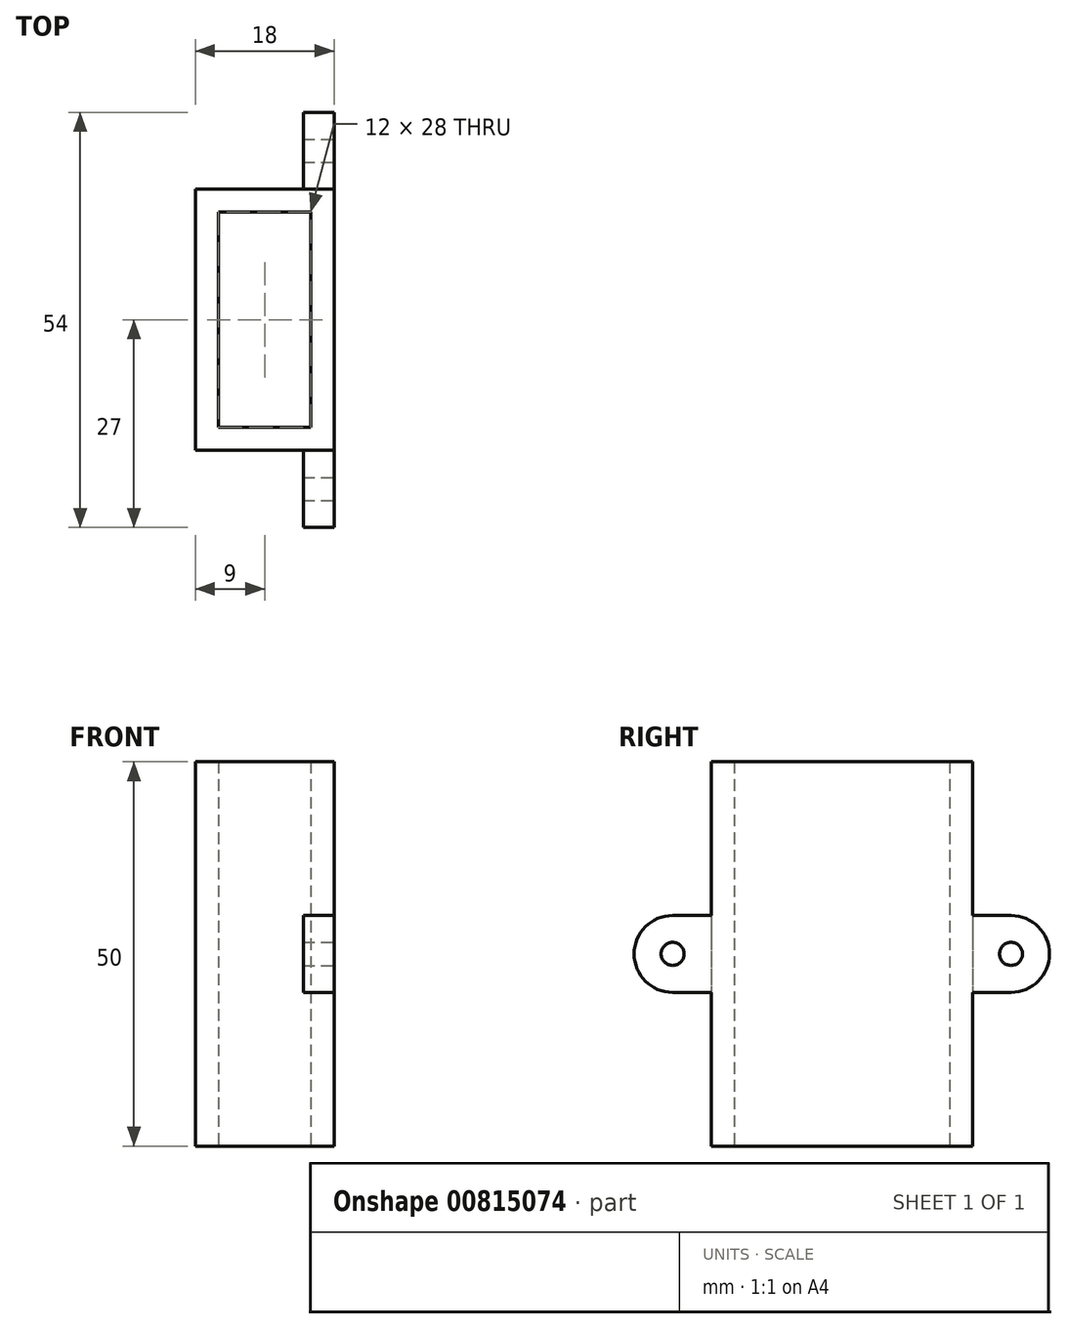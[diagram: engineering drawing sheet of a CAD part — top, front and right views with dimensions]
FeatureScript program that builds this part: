
annotation { "Feature Type Name" : "Feature", "Feature Type Description" : "" }
export const myFeature = defineFeature(function(context is Context, id is Id, definition is map)
    precondition{}
    {
        {
            var Q0;
            Q0=qCreatedBy(makeId("Top.planeOp"),FACE);
            var sketch = newSketch(context, id + "F0", { "sketchPlane" : qUnion([Q0])});
            skLineSegment(sketch, "E0.bottom", {"start": v(6, -14) * mm, "end": v(-6, -14) * mm});
            skLineSegment(sketch, "E0.top", {"start": v(6, 14) * mm, "end": v(-6, 14) * mm});
            skLineSegment(sketch, "E0.left", {"start": v(6, -14) * mm, "end": v(6, 14) * mm});
            skLineSegment(sketch, "E0.right", {"start": v(-6, -14) * mm, "end": v(-6, 14) * mm});
            skPoint(sketch, "E0.middle", {"position": v(0, 0) * mm});
            skLineSegment(sketch, "E1.bottom", {"start": v(9, -17) * mm, "end": v(-9, -17) * mm});
            skLineSegment(sketch, "E1.top", {"start": v(9, 17) * mm, "end": v(-9, 17) * mm});
            skLineSegment(sketch, "E1.left", {"start": v(9, -17) * mm, "end": v(9, 17) * mm});
            skLineSegment(sketch, "E1.right", {"start": v(-9, -17) * mm, "end": v(-9, 17) * mm});
            skLineSegment(sketch, "E2.left", {"start": v(-9, -5) * mm, "end": v(-9, 5) * mm});
            skLineSegment(sketch, "E3.left", {"start": v(9, 5) * mm, "end": v(9, -5) * mm});
            skSolve(sketch);
        }
        {
            var Q0;
            Q0=makeQuery(id+"F0.imprint","IMPRINT",FACE,{"disambiguationData":[TD([[makeQuery(id+"F0.imprint","IMPRINT",EDGE,{"derivedFrom":sQuery(id+"F0.wireOp",EDGE,"E0.bottom")}),1.0]])]});
            extrude(context, id + "F1", {"entities" : qUnion([Q0]), "depth" : 50 * mm, "offsetDistance" : 25 * mm});
        }
        {
            var Q0;
            Q0=makeQuery(id+"F1.opExtrude","SWEPT_FACE",FACE,{"disambiguationData":[OSD([sQuery(id+"F0.wireOp",EDGE,"E1.left"),sQuery(id+"F0.wireOp",EDGE,"E3.left")])]});
            var sketch = newSketch(context, id + "F2", { "sketchPlane" : qUnion([Q0])});
            skLineSegment(sketch, "E4", {"start": v(-17, 25) * mm, "end": v(17, 25) * mm, "construction": true});
            skLineSegment(sketch, "E5", {"start": v(-17, 30) * mm, "end": v(17, 30) * mm, "construction": true});
            skLineSegment(sketch, "E6", {"start": v(-17, 20) * mm, "end": v(17, 20) * mm, "construction": true});
            skLineSegment(sketch, "E7.bottom", {"start": v(17, 30) * mm, "end": v(27, 30) * mm});
            skLineSegment(sketch, "E7.top", {"start": v(17, 20) * mm, "end": v(27, 20) * mm});
            skLineSegment(sketch, "E7.left", {"start": v(17, 30) * mm, "end": v(17, 20) * mm});
            skLineSegment(sketch, "E7.right", {"start": v(27, 30) * mm, "end": v(27, 20) * mm});
            skLineSegment(sketch, "E8.bottom", {"start": v(-17, 30) * mm, "end": v(-27, 30) * mm});
            skLineSegment(sketch, "E8.top", {"start": v(-17, 20) * mm, "end": v(-27, 20) * mm});
            skLineSegment(sketch, "E8.left", {"start": v(-17, 30) * mm, "end": v(-17, 20) * mm});
            skLineSegment(sketch, "E8.right", {"start": v(-27, 30) * mm, "end": v(-27, 20) * mm});
            skLineSegment(sketch, "E9", {"start": v(-22, 30) * mm, "end": v(-22, 20) * mm, "construction": true});
            skLineSegment(sketch, "E10", {"start": v(-27, 25) * mm, "end": v(-17, 25) * mm, "construction": true});
            skLineSegment(sketch, "E11", {"start": v(22, 30) * mm, "end": v(22, 20) * mm, "construction": true});
            skLineSegment(sketch, "E12", {"start": v(27, 25) * mm, "end": v(17, 25) * mm, "construction": true});
            skCircle(sketch, "E13", {"center": v(-22, 25) * mm, "radius": 1.5 * mm});
            skCircle(sketch, "E14", {"center": v(22, 25) * mm, "radius": 1.5 * mm});
            skSolve(sketch);
        }
        {
            var Q0;
            Q0=makeQuery(id+"F2.imprint","IMPRINT",FACE,{"disambiguationData":[TD([[makeQuery(id+"F2.imprint","IMPRINT",EDGE,{"derivedFrom":sQuery(id+"F2.wireOp",EDGE,"E8.bottom")}),1.0]])]});
            var Q1;
            Q1=makeQuery(id+"F2.imprint","IMPRINT",FACE,{"disambiguationData":[TD([[makeQuery(id+"F2.imprint","IMPRINT",EDGE,{"derivedFrom":sQuery(id+"F2.wireOp",EDGE,"E7.bottom")}),-1.0]])]});
            extrude(context, id + "F3", {"entities" : qUnion([Q0, Q1]), "operationType" : NewBodyOperationType.ADD, "oppositeDirection" : true, "depth" : 4 * mm, "offsetDistance" : 25 * mm});
        }
        {
            var Q0;
            Q0=makeQuery(id+"F3.opExtrude","SWEPT_EDGE",EDGE,{"disambiguationData":[OSD([sQuery(id+"F2.wireOp",EDGE,"E7.top"),sQuery(id+"F2.wireOp",EDGE,"E7.right")])]});
            var Q1;
            Q1=makeQuery(id+"F3.opExtrude","SWEPT_EDGE",EDGE,{"disambiguationData":[OSD([sQuery(id+"F2.wireOp",EDGE,"E7.bottom"),sQuery(id+"F2.wireOp",EDGE,"E7.right")])]});
            fillet(context, id + "F4", {"entities" : qUnion([Q0, Q1]), "radius" : 5 * mm, "tangentPropagation" : true, "allowEdgeOverflow" : false});
        }
        {
            var Q0;
            Q0=makeQuery(id+"F3.opExtrude","SWEPT_EDGE",EDGE,{"disambiguationData":[OSD([sQuery(id+"F2.wireOp",EDGE,"E8.top"),sQuery(id+"F2.wireOp",EDGE,"E8.right")])]});
            var Q1;
            Q1=makeQuery(id+"F3.opExtrude","SWEPT_EDGE",EDGE,{"disambiguationData":[OSD([sQuery(id+"F2.wireOp",EDGE,"E8.bottom"),sQuery(id+"F2.wireOp",EDGE,"E8.right")])]});
            fillet(context, id + "F5", {"entities" : qUnion([Q0, Q1]), "radius" : 5 * mm, "tangentPropagation" : true, "allowEdgeOverflow" : false});
        }
    });
